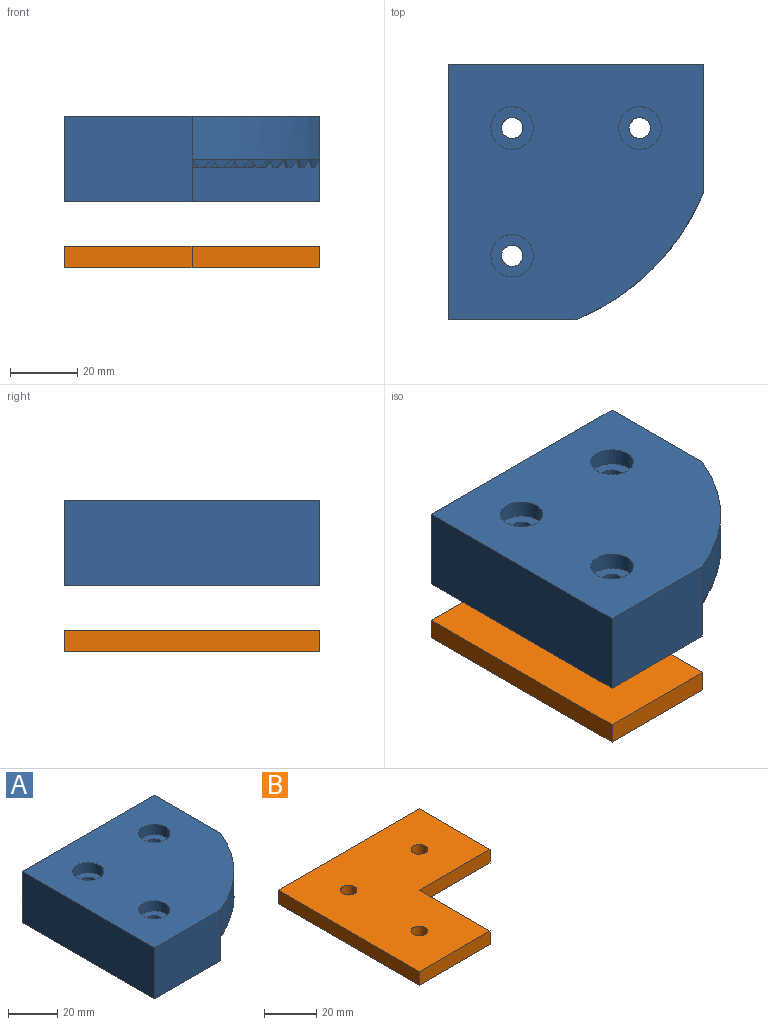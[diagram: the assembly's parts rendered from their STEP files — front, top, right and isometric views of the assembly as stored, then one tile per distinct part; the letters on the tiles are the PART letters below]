
ASSEMBLY  parts=2 mates=2
PART A: 233 faces, bbox 76.2x76.2x25.4 mm
  f0: cylinder r=3.17mm len=20.32mm, axis (0,0,-1), area 405.4mm2, adj f16,f232
  f1: cylinder r=3.17mm len=20.32mm, axis (0,0,-1), area 405.4mm2, adj f16,f230
  f2: cylinder r=3.17mm len=20.32mm, axis (0,0,-1), area 405.4mm2, adj f16,f228
  f3: plane 38.1x31.93mm, normal (0,0,-1), area 584mm2, adj f21,f22,f23,f29,f30,f33,f34,f37
  f4: plane 0.46x0.22mm, normal (0,0,-1), area 0mm2, adj f21,f84,f112
  f5: plane 6.09x4.03mm, normal (0,0,-1), area 8mm2, adj f21,f25,f26,f56,f85
  f6: plane 5.03x3.44mm, normal (0,0,-1), area 6.3mm2, adj f23,f26,f29,f57
  f7: plane 5.74x2.65mm, normal (0,0,-1), area 0.3mm2, adj f23,f52
  f8: plane 5.45x3.21mm, normal (0,0,-1), area 0.3mm2, adj f23,f48
  f9: plane 5.1x3.75mm, normal (0,0,-1), area 0.3mm2, adj f23,f44
  f10: plane 4.69x4.24mm, normal (0,0,-1), area 0.3mm2, adj f23,f40
  f11: plane 4.69x4.24mm, normal (0,0,-1), area 0.3mm2, adj f23,f36
  f12: plane 5.1x3.75mm, normal (0,0,-1), area 0.3mm2, adj f23,f32
  f13: plane 5.45x3.21mm, normal (0,0,-1), area 0.3mm2, adj f23,f28
  f14: plane 5.74x2.65mm, normal (0,0,-1), area 0.3mm2, adj f23,f24
  f15: plane 76.2x76.2mm, normal (0,0,1), area 4898.1mm2, adj f17,f18,f19,f20,f23,f227,f229,f231
  f16: plane 76.2x76.2mm, normal (0,0,-1), area 4259.8mm2, adj f0,f1,f2,f17,f18,f19,f20,f21
  f17: plane 38.1x25.4mm, normal (0,-1,0), area 967.7mm2, adj f15,f16,f20,f21,f23
  f18: plane 38.1x25.4mm, normal (1,0,0), area 967.7mm2, adj f15,f16,f19,f22,f23
  f19: plane 76.2x25.4mm, normal (0,1,0), area 1935.5mm2, adj f15,f16,f18,f20
  f20: plane 76.2x25.4mm, normal (-1,0,0), area 1935.5mm2, adj f15,f16,f17,f19
  f21: plane 38.1x12.7mm, normal (1,0,0), area 474.6mm2, adj f3,f4,f5,f16,f17,f22,f84,f85
  f22: plane 38.1x12.7mm, normal (0,-1,0), area 483.9mm2, adj f3,f16,f18,f21
  f23: cylinder r=69.28mm len=38.1mm, axis (0,0,-1), area 702.8mm2, adj f3,f6,f7,f8,f9,f10,f11,f12
  f24: plane 5.74x2.65mm, normal (0.4,-0.88,-0.26), area 10.8mm2, adj f14,f25,f26,f27
  f25: plane 3.25x2.54mm, normal (-0.82,0.5,-0.26), area 6.5mm2, adj f5,f24,f26,f27
  f26: plane 3.76x2.54mm, normal (0.15,0.95,-0.26), area 6.5mm2, adj f5,f6,f24,f25,f27,f56,f57
  f27: plane 1.69x0.96mm, normal (0,0,-1), area 0.6mm2, adj f24,f25,f26
  f28: plane 5.45x3.21mm, normal (0.49,-0.83,-0.26), area 10.8mm2, adj f13,f29,f30,f31
  f29: plane 3.44x2.54mm, normal (-0.87,0.42,-0.26), area 6.5mm2, adj f3,f6,f28,f30,f31,f57,f58
  f30: plane 3.8x2.54mm, normal (0.06,0.96,-0.26), area 6.5mm2, adj f3,f28,f29,f31
  f31: plane 1.6x1.01mm, normal (0,0,-1), area 0.6mm2, adj f28,f29,f30
  f32: plane 5.1x3.75mm, normal (0.57,-0.78,-0.26), area 10.8mm2, adj f12,f33,f34,f35
  f33: plane 3.59x2.54mm, normal (-0.91,0.33,-0.26), area 6.5mm2, adj f3,f32,f34,f35
  f34: plane 3.81x2.54mm, normal (-0.04,0.97,-0.26), area 6.5mm2, adj f3,f32,f33,f35
  f35: plane 1.5x1.1mm, normal (0,0,-1), area 0.6mm2, adj f32,f33,f34
  f36: plane 4.69x4.24mm, normal (0.65,-0.72,-0.26), area 10.8mm2, adj f11,f37,f38,f39
  f37: plane 3.7x2.54mm, normal (-0.94,0.23,-0.26), area 6.5mm2, adj f3,f36,f38,f39
  f38: plane 3.77x2.54mm, normal (-0.14,0.96,-0.26), area 6.5mm2, adj f3,f36,f37,f39
  f39: plane 1.38x1.25mm, normal (0,0,-1), area 0.6mm2, adj f36,f37,f38
  f40: plane 4.69x4.24mm, normal (0.72,-0.65,-0.26), area 10.8mm2, adj f10,f41,f42,f43
  f41: plane 3.77x2.54mm, normal (-0.96,0.14,-0.26), area 6.5mm2, adj f3,f40,f42,f43
  f42: plane 3.7x2.54mm, normal (-0.23,0.94,-0.26), area 6.5mm2, adj f3,f40,f41,f43
  f43: plane 1.38x1.25mm, normal (0,0,-1), area 0.6mm2, adj f40,f41,f42
  f44: plane 5.1x3.75mm, normal (0.78,-0.57,-0.26), area 10.8mm2, adj f9,f45,f46,f47
  f45: plane 3.81x2.54mm, normal (-0.97,0.04,-0.26), area 6.5mm2, adj f3,f44,f46,f47
  f46: plane 3.59x2.54mm, normal (-0.33,0.91,-0.26), area 6.5mm2, adj f3,f44,f45,f47
  f47: plane 1.5x1.1mm, normal (0,0,-1), area 0.6mm2, adj f44,f45,f46
  f48: plane 5.45x3.21mm, normal (0.83,-0.49,-0.26), area 10.8mm2, adj f8,f49,f50,f51
  f49: plane 3.8x2.54mm, normal (-0.96,-0.06,-0.26), area 6.5mm2, adj f3,f48,f50,f51
  f50: plane 3.44x2.54mm, normal (-0.42,0.87,-0.26), area 6.5mm2, adj f3,f48,f49,f51
  f51: plane 1.6x1.01mm, normal (0,0,-1), area 0.6mm2, adj f48,f49,f50
  f52: plane 5.74x2.65mm, normal (0.88,-0.4,-0.26), area 10.8mm2, adj f7,f53,f54,f55
  f53: plane 3.76x2.54mm, normal (-0.95,-0.15,-0.26), area 6.5mm2, adj f3,f52,f54,f55
  f54: plane 3.25x2.54mm, normal (-0.5,0.82,-0.26), area 6.5mm2, adj f3,f52,f53,f55
  f55: plane 1.69x0.96mm, normal (0,0,-1), area 0.6mm2, adj f52,f53,f54
  f56: plane 3.3x2.54mm, normal (-0.87,0.42,-0.26), area 6.5mm2, adj f3,f5,f26,f57,f58,f59,f85,f86
  f57: plane 5.24x3.06mm, normal (0.49,-0.83,-0.26), area 10.7mm2, adj f6,f26,f29,f56,f58,f59
  f58: plane 3.72x2.54mm, normal (0.06,0.96,-0.26), area 6.5mm2, adj f3,f29,f56,f57,f59
  f59: plane 1.6x1.01mm, normal (0,0,-1), area 0.6mm2, adj f56,f57,f58
  f60: plane 5.1x3.75mm, normal (0.57,-0.78,-0.26), area 10.8mm2, adj f3,f61,f62,f63
  f61: plane 3.59x2.54mm, normal (-0.91,0.33,-0.26), area 6.5mm2, adj f3,f60,f62,f63
  f62: plane 3.81x2.54mm, normal (-0.04,0.97,-0.26), area 6.5mm2, adj f3,f60,f61,f63
  f63: plane 1.5x1.1mm, normal (0,0,-1), area 0.6mm2, adj f60,f61,f62
  f64: plane 4.69x4.24mm, normal (0.65,-0.72,-0.26), area 10.8mm2, adj f3,f65,f66,f67
  f65: plane 3.7x2.54mm, normal (-0.94,0.23,-0.26), area 6.5mm2, adj f3,f64,f66,f67
  f66: plane 3.77x2.54mm, normal (-0.14,0.96,-0.26), area 6.5mm2, adj f3,f64,f65,f67
  f67: plane 1.38x1.25mm, normal (0,0,-1), area 0.6mm2, adj f64,f65,f66
  f68: plane 4.69x4.24mm, normal (0.72,-0.65,-0.26), area 10.8mm2, adj f3,f69,f70,f71
  f69: plane 3.77x2.54mm, normal (-0.96,0.14,-0.26), area 6.5mm2, adj f3,f68,f70,f71
  f70: plane 3.7x2.54mm, normal (-0.23,0.94,-0.26), area 6.5mm2, adj f3,f68,f69,f71
  f71: plane 1.38x1.25mm, normal (0,0,-1), area 0.6mm2, adj f68,f69,f70
  f72: plane 5.1x3.75mm, normal (0.78,-0.57,-0.26), area 10.8mm2, adj f3,f73,f74,f75
  f73: plane 3.81x2.54mm, normal (-0.97,0.04,-0.26), area 6.5mm2, adj f3,f72,f74,f75
  f74: plane 3.59x2.54mm, normal (-0.33,0.91,-0.26), area 6.5mm2, adj f3,f72,f73,f75
  f75: plane 1.5x1.1mm, normal (0,0,-1), area 0.6mm2, adj f72,f73,f74
  f76: plane 5.45x3.21mm, normal (0.83,-0.49,-0.26), area 10.8mm2, adj f3,f77,f78,f79
  f77: plane 3.8x2.54mm, normal (-0.96,-0.06,-0.26), area 6.5mm2, adj f3,f76,f78,f79
  f78: plane 3.44x2.54mm, normal (-0.42,0.87,-0.26), area 6.5mm2, adj f3,f76,f77,f79
  f79: plane 1.6x1.01mm, normal (0,0,-1), area 0.6mm2, adj f76,f77,f78
  f80: plane 5.74x2.65mm, normal (0.88,-0.4,-0.26), area 10.8mm2, adj f3,f81,f82,f83
  f81: plane 3.76x2.54mm, normal (-0.95,-0.15,-0.26), area 6.5mm2, adj f3,f80,f82,f83
  f82: plane 3.25x2.54mm, normal (-0.5,0.82,-0.26), area 6.5mm2, adj f3,f80,f81,f83
  f83: plane 1.69x0.96mm, normal (0,0,-1), area 0.6mm2, adj f80,f81,f82
  f84: plane 2.54x2.04mm, normal (-0.87,0.42,-0.26), area 3.3mm2, adj f3,f4,f21,f85,f86,f87,f112,f113
  f85: plane 4.09x2.54mm, normal (0.49,-0.83,-0.26), area 9.2mm2, adj f5,f21,f56,f84,f86,f87
  f86: plane 3.72x2.54mm, normal (0.06,0.96,-0.26), area 6.5mm2, adj f3,f56,f84,f85,f87
  f87: plane 1.6x1.01mm, normal (0,0,-1), area 0.6mm2, adj f84,f85,f86
  f88: plane 5.1x3.75mm, normal (0.57,-0.78,-0.26), area 10.8mm2, adj f3,f89,f90,f91
  f89: plane 3.59x2.54mm, normal (-0.91,0.33,-0.26), area 6.5mm2, adj f3,f88,f90,f91
  f90: plane 3.81x2.54mm, normal (-0.04,0.97,-0.26), area 6.5mm2, adj f3,f88,f89,f91
  f91: plane 1.5x1.1mm, normal (0,0,-1), area 0.6mm2, adj f88,f89,f90
  f92: plane 4.69x4.24mm, normal (0.65,-0.72,-0.26), area 10.8mm2, adj f3,f93,f94,f95
  f93: plane 3.7x2.54mm, normal (-0.94,0.23,-0.26), area 6.5mm2, adj f3,f92,f94,f95
  f94: plane 3.77x2.54mm, normal (-0.14,0.96,-0.26), area 6.5mm2, adj f3,f92,f93,f95
  f95: plane 1.38x1.25mm, normal (0,0,-1), area 0.6mm2, adj f92,f93,f94
  f96: plane 4.69x4.24mm, normal (0.72,-0.65,-0.26), area 10.8mm2, adj f3,f97,f98,f99
  f97: plane 3.77x2.54mm, normal (-0.96,0.14,-0.26), area 6.5mm2, adj f3,f96,f98,f99
  f98: plane 3.7x2.54mm, normal (-0.23,0.94,-0.26), area 6.5mm2, adj f3,f96,f97,f99
  f99: plane 1.38x1.25mm, normal (0,0,-1), area 0.6mm2, adj f96,f97,f98
  f100: plane 5.1x3.75mm, normal (0.78,-0.57,-0.26), area 10.8mm2, adj f3,f101,f102,f103
  f101: plane 3.81x2.54mm, normal (-0.97,0.04,-0.26), area 6.5mm2, adj f3,f100,f102,f103
  f102: plane 3.59x2.54mm, normal (-0.33,0.91,-0.26), area 6.5mm2, adj f3,f100,f101,f103
  f103: plane 1.5x1.1mm, normal (0,0,-1), area 0.6mm2, adj f100,f101,f102
  f104: plane 5.45x3.21mm, normal (0.83,-0.49,-0.26), area 10.8mm2, adj f3,f105,f106,f107
  f105: plane 3.8x2.54mm, normal (-0.96,-0.06,-0.26), area 6.5mm2, adj f3,f104,f106,f107
  f106: plane 3.44x2.54mm, normal (-0.42,0.87,-0.26), area 6.5mm2, adj f3,f104,f105,f107
  f107: plane 1.6x1.01mm, normal (0,0,-1), area 0.6mm2, adj f104,f105,f106
  f108: plane 5.74x2.65mm, normal (0.88,-0.4,-0.26), area 10.8mm2, adj f3,f109,f110,f111
  f109: plane 3.76x2.54mm, normal (-0.95,-0.15,-0.26), area 6.5mm2, adj f3,f108,f110,f111
  f110: plane 3.25x2.54mm, normal (-0.5,0.82,-0.26), area 6.5mm2, adj f3,f108,f109,f111
  f111: plane 1.69x0.96mm, normal (0,0,-1), area 0.6mm2, adj f108,f109,f110
  f112: plane 0.4x0.28mm, normal (0.49,-0.83,-0.26), area 0.1mm2, adj f4,f21,f84,f113
  f113: plane 0.4x0.28mm, normal (0.06,0.96,-0.26), area 0.1mm2, adj f3,f21,f84,f112
  f114: plane 5.1x3.75mm, normal (0.57,-0.78,-0.26), area 10.8mm2, adj f3,f115,f116,f117
  f115: plane 3.59x2.54mm, normal (-0.91,0.33,-0.26), area 6.5mm2, adj f3,f114,f116,f117
  f116: plane 3.81x2.54mm, normal (-0.04,0.97,-0.26), area 6.5mm2, adj f3,f114,f115,f117
  f117: plane 1.5x1.1mm, normal (0,0,-1), area 0.6mm2, adj f114,f115,f116
  f118: plane 4.69x4.24mm, normal (0.65,-0.72,-0.26), area 10.8mm2, adj f3,f119,f120,f121
  f119: plane 3.7x2.54mm, normal (-0.94,0.23,-0.26), area 6.5mm2, adj f3,f118,f120,f121
  f120: plane 3.77x2.54mm, normal (-0.14,0.96,-0.26), area 6.5mm2, adj f3,f118,f119,f121
  f121: plane 1.38x1.25mm, normal (0,0,-1), area 0.6mm2, adj f118,f119,f120
  f122: plane 4.69x4.24mm, normal (0.72,-0.65,-0.26), area 10.8mm2, adj f3,f123,f124,f125
  f123: plane 3.77x2.54mm, normal (-0.96,0.14,-0.26), area 6.5mm2, adj f3,f122,f124,f125
  f124: plane 3.7x2.54mm, normal (-0.23,0.94,-0.26), area 6.5mm2, adj f3,f122,f123,f125
  f125: plane 1.38x1.25mm, normal (0,0,-1), area 0.6mm2, adj f122,f123,f124
  f126: plane 5.1x3.75mm, normal (0.78,-0.57,-0.26), area 10.8mm2, adj f3,f127,f128,f129
  f127: plane 3.81x2.54mm, normal (-0.97,0.04,-0.26), area 6.5mm2, adj f3,f126,f128,f129
  f128: plane 3.59x2.54mm, normal (-0.33,0.91,-0.26), area 6.5mm2, adj f3,f126,f127,f129
  f129: plane 1.5x1.1mm, normal (0,0,-1), area 0.6mm2, adj f126,f127,f128
  f130: plane 5.45x3.21mm, normal (0.83,-0.49,-0.26), area 10.8mm2, adj f3,f131,f132,f133
  f131: plane 3.8x2.54mm, normal (-0.96,-0.06,-0.26), area 6.5mm2, adj f3,f130,f132,f133
  f132: plane 3.44x2.54mm, normal (-0.42,0.87,-0.26), area 6.5mm2, adj f3,f130,f131,f133
  f133: plane 1.6x1.01mm, normal (0,0,-1), area 0.6mm2, adj f130,f131,f132
  f134: plane 5.74x2.65mm, normal (0.88,-0.4,-0.26), area 10.8mm2, adj f3,f135,f136,f137
  f135: plane 3.76x2.54mm, normal (-0.95,-0.15,-0.26), area 6.5mm2, adj f3,f134,f136,f137
  f136: plane 3.25x2.54mm, normal (-0.5,0.82,-0.26), area 6.5mm2, adj f3,f134,f135,f137
  f137: plane 1.69x0.96mm, normal (0,0,-1), area 0.6mm2, adj f134,f135,f136
  f138: plane 2.54x2.21mm, normal (0.57,-0.78,-0.26), area 3.6mm2, adj f3,f21,f139,f140
  f139: plane 2.54x2.21mm, normal (-0.04,0.97,-0.26), area 2.9mm2, adj f3,f21,f138,f140
  f140: plane 0.01x0.01mm, normal (0,0,-1), area 0mm2, adj f21,f138,f139
  f141: plane 4.69x4.24mm, normal (0.65,-0.72,-0.26), area 10.8mm2, adj f3,f142,f143,f144
  f142: plane 3.7x2.54mm, normal (-0.94,0.23,-0.26), area 6.5mm2, adj f3,f141,f143,f144
  f143: plane 3.77x2.54mm, normal (-0.14,0.96,-0.26), area 6.5mm2, adj f3,f141,f142,f144
  f144: plane 1.38x1.25mm, normal (0,0,-1), area 0.6mm2, adj f141,f142,f143
  f145: plane 4.69x4.24mm, normal (0.72,-0.65,-0.26), area 10.8mm2, adj f3,f146,f147,f148
  f146: plane 3.77x2.54mm, normal (-0.96,0.14,-0.26), area 6.5mm2, adj f3,f145,f147,f148
  f147: plane 3.7x2.54mm, normal (-0.23,0.94,-0.26), area 6.5mm2, adj f3,f145,f146,f148
  f148: plane 1.38x1.25mm, normal (0,0,-1), area 0.6mm2, adj f145,f146,f147
  f149: plane 5.1x3.75mm, normal (0.78,-0.57,-0.26), area 10.8mm2, adj f3,f150,f151,f152
  f150: plane 3.81x2.54mm, normal (-0.97,0.04,-0.26), area 6.5mm2, adj f3,f149,f151,f152
  f151: plane 3.59x2.54mm, normal (-0.33,0.91,-0.26), area 6.5mm2, adj f3,f149,f150,f152
  f152: plane 1.5x1.1mm, normal (0,0,-1), area 0.6mm2, adj f149,f150,f151
  f153: plane 5.45x3.21mm, normal (0.83,-0.49,-0.26), area 10.8mm2, adj f3,f154,f155,f156
  f154: plane 3.8x2.54mm, normal (-0.96,-0.06,-0.26), area 6.5mm2, adj f3,f153,f155,f156
  f155: plane 3.44x2.54mm, normal (-0.42,0.87,-0.26), area 6.5mm2, adj f3,f153,f154,f156
  f156: plane 1.6x1.01mm, normal (0,0,-1), area 0.6mm2, adj f153,f154,f155
  f157: plane 5.74x2.65mm, normal (0.88,-0.4,-0.26), area 10.8mm2, adj f3,f158,f159,f160
  f158: plane 3.76x2.54mm, normal (-0.95,-0.15,-0.26), area 6.5mm2, adj f3,f157,f159,f160
  f159: plane 3.25x2.54mm, normal (-0.5,0.82,-0.26), area 6.5mm2, adj f3,f157,f158,f160
  f160: plane 1.69x0.96mm, normal (0,0,-1), area 0.6mm2, adj f157,f158,f159
  f161: plane 3.62x3.27mm, normal (0.65,-0.72,-0.26), area 9mm2, adj f3,f21,f162,f163,f164
  f162: plane 1.82x1.73mm, normal (-0.94,0.23,-0.26), area 1.5mm2, adj f21,f161,f163,f164
  f163: plane 3.62x2.54mm, normal (-0.14,0.96,-0.26), area 6.4mm2, adj f3,f21,f161,f162,f164
  f164: plane 1.38x1.25mm, normal (0,0,-1), area 0.6mm2, adj f161,f162,f163
  f165: plane 4.69x4.24mm, normal (0.72,-0.65,-0.26), area 10.8mm2, adj f3,f166,f167,f168
  f166: plane 3.77x2.54mm, normal (-0.96,0.14,-0.26), area 6.5mm2, adj f3,f165,f167,f168
  f167: plane 3.7x2.54mm, normal (-0.23,0.94,-0.26), area 6.5mm2, adj f3,f165,f166,f168
  f168: plane 1.38x1.25mm, normal (0,0,-1), area 0.6mm2, adj f165,f166,f167
  f169: plane 5.1x3.75mm, normal (0.78,-0.57,-0.26), area 10.8mm2, adj f3,f170,f171,f172
  f170: plane 3.81x2.54mm, normal (-0.97,0.04,-0.26), area 6.5mm2, adj f3,f169,f171,f172
  f171: plane 3.59x2.54mm, normal (-0.33,0.91,-0.26), area 6.5mm2, adj f3,f169,f170,f172
  f172: plane 1.5x1.1mm, normal (0,0,-1), area 0.6mm2, adj f169,f170,f171
  f173: plane 5.45x3.21mm, normal (0.83,-0.49,-0.26), area 10.8mm2, adj f3,f174,f175,f176
  f174: plane 3.8x2.54mm, normal (-0.96,-0.06,-0.26), area 6.5mm2, adj f3,f173,f175,f176
  f175: plane 3.44x2.54mm, normal (-0.42,0.87,-0.26), area 6.5mm2, adj f3,f173,f174,f176
  f176: plane 1.6x1.01mm, normal (0,0,-1), area 0.6mm2, adj f173,f174,f175
  f177: plane 5.74x2.65mm, normal (0.88,-0.4,-0.26), area 10.8mm2, adj f3,f178,f179,f180
  f178: plane 3.76x2.54mm, normal (-0.95,-0.15,-0.26), area 6.5mm2, adj f3,f177,f179,f180
  f179: plane 3.25x2.54mm, normal (-0.5,0.82,-0.26), area 6.5mm2, adj f3,f177,f178,f180
  f180: plane 1.69x0.96mm, normal (0,0,-1), area 0.6mm2, adj f177,f178,f179
  f181: plane 4.69x4.24mm, normal (0.72,-0.65,-0.26), area 10.8mm2, adj f3,f182,f183,f184
  f182: plane 3.77x2.54mm, normal (-0.96,0.14,-0.26), area 6.5mm2, adj f3,f181,f183,f184
  f183: plane 3.7x2.54mm, normal (-0.23,0.94,-0.26), area 6.5mm2, adj f3,f181,f182,f184
  f184: plane 1.38x1.25mm, normal (0,0,-1), area 0.6mm2, adj f181,f182,f183
  f185: plane 5.1x3.75mm, normal (0.78,-0.57,-0.26), area 10.8mm2, adj f3,f186,f187,f188
  f186: plane 3.81x2.54mm, normal (-0.97,0.04,-0.26), area 6.5mm2, adj f3,f185,f187,f188
  f187: plane 3.59x2.54mm, normal (-0.33,0.91,-0.26), area 6.5mm2, adj f3,f185,f186,f188
  f188: plane 1.5x1.1mm, normal (0,0,-1), area 0.6mm2, adj f185,f186,f187
  f189: plane 5.45x3.21mm, normal (0.83,-0.49,-0.26), area 10.8mm2, adj f3,f190,f191,f192
  f190: plane 3.8x2.54mm, normal (-0.96,-0.06,-0.26), area 6.5mm2, adj f3,f189,f191,f192
  f191: plane 3.44x2.54mm, normal (-0.42,0.87,-0.26), area 6.5mm2, adj f3,f189,f190,f192
  f192: plane 1.6x1.01mm, normal (0,0,-1), area 0.6mm2, adj f189,f190,f191
  f193: plane 5.74x2.65mm, normal (0.88,-0.4,-0.26), area 10.8mm2, adj f3,f194,f195,f196
  f194: plane 3.76x2.54mm, normal (-0.95,-0.15,-0.26), area 6.5mm2, adj f3,f193,f195,f196
  f195: plane 3.25x2.54mm, normal (-0.5,0.82,-0.26), area 6.5mm2, adj f3,f193,f194,f196
  f196: plane 1.69x0.96mm, normal (0,0,-1), area 0.6mm2, adj f193,f194,f195
  f197: plane 0.91x0.79mm, normal (0.72,-0.65,-0.26), area 0.5mm2, adj f3,f21,f198
  f198: plane 0.91x0.71mm, normal (-0.23,0.94,-0.26), area 0.3mm2, adj f3,f21,f197
  f199: plane 5.1x3.75mm, normal (0.78,-0.57,-0.26), area 10.8mm2, adj f3,f200,f201,f202
  f200: plane 3.81x2.54mm, normal (-0.97,0.04,-0.26), area 6.5mm2, adj f3,f199,f201,f202
  f201: plane 3.59x2.54mm, normal (-0.33,0.91,-0.26), area 6.5mm2, adj f3,f199,f200,f202
  f202: plane 1.5x1.1mm, normal (0,0,-1), area 0.6mm2, adj f199,f200,f201
  f203: plane 5.45x3.21mm, normal (0.83,-0.49,-0.26), area 10.8mm2, adj f3,f204,f205,f206
  f204: plane 3.8x2.54mm, normal (-0.96,-0.06,-0.26), area 6.5mm2, adj f3,f203,f205,f206
  f205: plane 3.44x2.54mm, normal (-0.42,0.87,-0.26), area 6.5mm2, adj f3,f203,f204,f206
  f206: plane 1.6x1.01mm, normal (0,0,-1), area 0.6mm2, adj f203,f204,f205
  f207: plane 5.74x2.65mm, normal (0.88,-0.4,-0.26), area 10.8mm2, adj f3,f208,f209,f210
  f208: plane 3.76x2.54mm, normal (-0.95,-0.15,-0.26), area 6.5mm2, adj f3,f207,f209,f210
  f209: plane 3.25x2.54mm, normal (-0.5,0.82,-0.26), area 6.5mm2, adj f3,f207,f208,f210
  f210: plane 1.69x0.96mm, normal (0,0,-1), area 0.6mm2, adj f207,f208,f209
  f211: plane 1.47x1.46mm, normal (0.78,-0.57,-0.26), area 1.4mm2, adj f3,f21,f212
  f212: plane 1.46x1.08mm, normal (-0.33,0.91,-0.26), area 0.9mm2, adj f3,f21,f211
  f213: plane 5.45x3.21mm, normal (0.83,-0.49,-0.26), area 10.8mm2, adj f3,f214,f215,f216
  f214: plane 3.8x2.54mm, normal (-0.96,-0.06,-0.26), area 6.5mm2, adj f3,f213,f215,f216
  f215: plane 3.44x2.54mm, normal (-0.42,0.87,-0.26), area 6.5mm2, adj f3,f213,f214,f216
  f216: plane 1.6x1.01mm, normal (0,0,-1), area 0.6mm2, adj f213,f214,f215
  f217: plane 5.74x2.65mm, normal (0.88,-0.4,-0.26), area 10.8mm2, adj f3,f218,f219,f220
  f218: plane 3.76x2.54mm, normal (-0.95,-0.15,-0.26), area 6.5mm2, adj f3,f217,f219,f220
  f219: plane 3.25x2.54mm, normal (-0.5,0.82,-0.26), area 6.5mm2, adj f3,f217,f218,f220
  f220: plane 1.69x0.96mm, normal (0,0,-1), area 0.6mm2, adj f217,f218,f219
  f221: plane 1.44x1.26mm, normal (0.83,-0.49,-0.26), area 1.1mm2, adj f3,f21,f222
  f222: plane 1.26x0.85mm, normal (-0.42,0.87,-0.26), area 0.6mm2, adj f3,f21,f221
  f223: plane 5.74x2.65mm, normal (0.88,-0.4,-0.26), area 10.8mm2, adj f3,f224,f225,f226
  f224: plane 3.76x2.54mm, normal (-0.95,-0.15,-0.26), area 6.5mm2, adj f3,f223,f225,f226
  f225: plane 3.25x2.54mm, normal (-0.5,0.82,-0.26), area 6.5mm2, adj f3,f223,f224,f226
  f226: plane 1.69x0.96mm, normal (0,0,-1), area 0.6mm2, adj f223,f224,f225
  f227: cylinder r=6.35mm len=12.7mm, axis (0,0,1), area 202.7mm2, adj f15,f228
  f228: plane 12.7x12.7mm, normal (0,0,1), area 95mm2, adj f2,f227
  f229: cylinder r=6.35mm len=12.7mm, axis (0,0,1), area 202.7mm2, adj f15,f230
  f230: plane 12.7x12.7mm, normal (0,0,1), area 95mm2, adj f1,f229
  f231: cylinder r=6.35mm len=12.7mm, axis (0,0,1), area 202.7mm2, adj f15,f232
  f232: plane 12.7x12.7mm, normal (0,0,1), area 95mm2, adj f0,f231
PART B: 11 faces, bbox 76.2x76.2x6.4 mm
  f0: plane 38.1x6.35mm, normal (0,-1,0), area 241.9mm2, adj f1,f8,f9,f10
  f1: plane 38.1x6.35mm, normal (1,0,0), area 241.9mm2, adj f0,f2,f9,f10
  f2: plane 38.1x6.35mm, normal (0,-1,0), area 241.9mm2, adj f1,f3,f9,f10
  f3: plane 76.2x6.35mm, normal (-1,0,0), area 483.9mm2, adj f2,f4,f9,f10
  f4: plane 76.2x6.35mm, normal (0,1,0), area 483.9mm2, adj f3,f8,f9,f10
  f5: cylinder r=3.17mm len=6.35mm, axis (0,0,1), area 126.7mm2, adj f9,f10
  f6: cylinder r=3.17mm len=6.35mm, axis (0,0,1), area 126.7mm2, adj f9,f10
  f7: cylinder r=3.17mm len=6.35mm, axis (0,0,1), area 126.7mm2, adj f9,f10
  f8: plane 38.1x6.35mm, normal (1,0,0), area 241.9mm2, adj f0,f4,f9,f10
  f9: plane 76.2x76.2mm, normal (0,0,-1), area 4259.8mm2, adj f0,f1,f2,f3,f4,f5,f6,f7
  f10: plane 76.2x76.2mm, normal (0,0,1), area 4259.8mm2, adj f0,f1,f2,f3,f4,f5,f6,f7
PLACE A t=(55.01,32.95,-139.94)mm
PLACE B t=(55.01,32.95,-102.45)mm
MATE slider A.f16 <-> B.f10  axis (0,0,-1) through (55.01,32.95,-139.94)mm
MATE parallel A.f16 <-> B.f10  axis (0,0,-1) through (55.01,32.95,-139.94)mm
